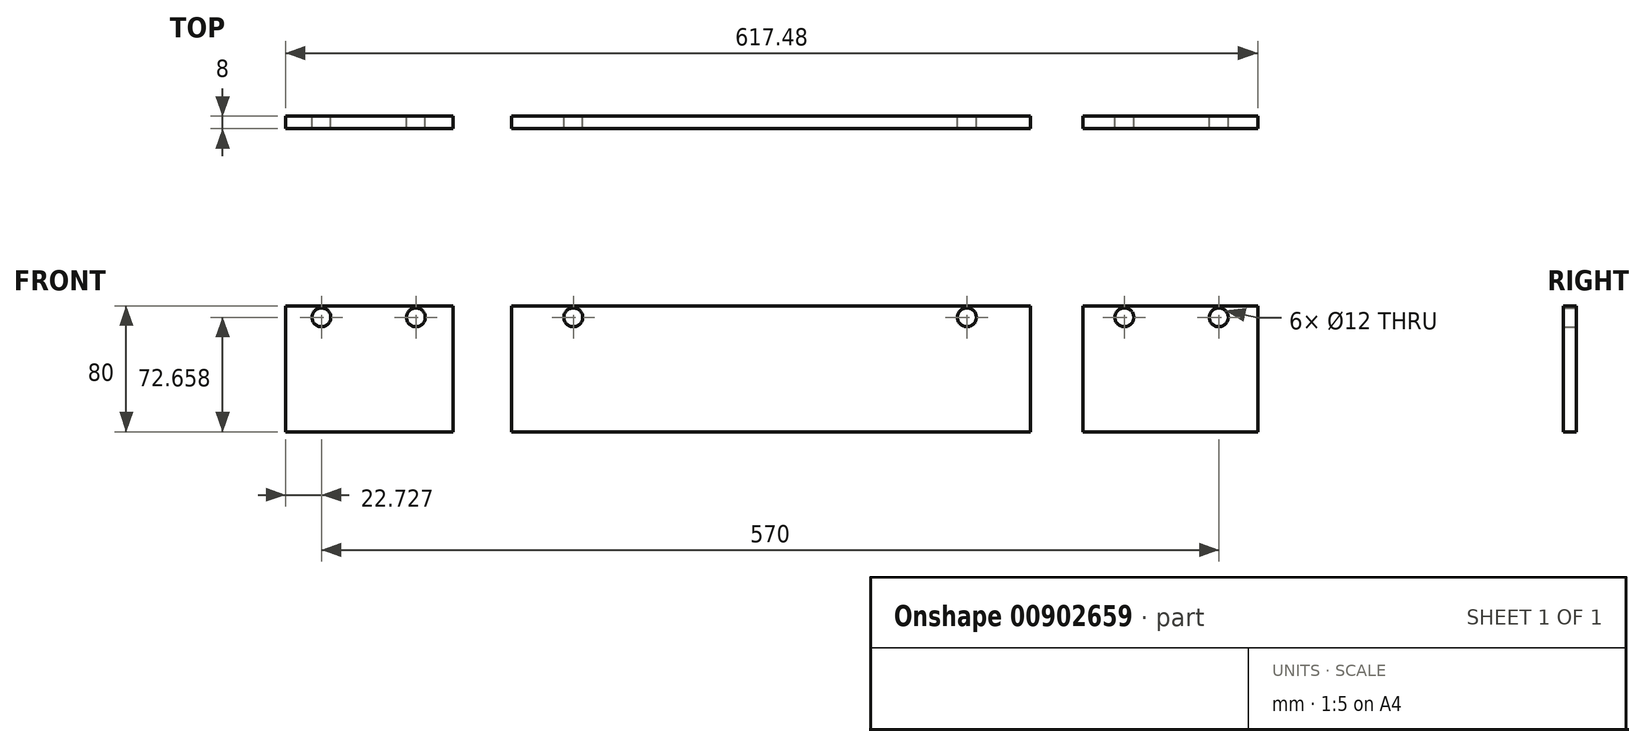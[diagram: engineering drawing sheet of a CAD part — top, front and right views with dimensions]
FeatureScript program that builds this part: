
annotation { "Feature Type Name" : "Feature", "Feature Type Description" : "" }
export const myFeature = defineFeature(function(context is Context, id is Id, definition is map)
    precondition{}
    {
        {
            var Q0;
            Q0=qCreatedBy(makeId("Front.planeOp"),FACE);
            var sketch = newSketch(context, id + "F0", { "sketchPlane" : qUnion([Q0])});
            skCircle(sketch, "E0", {"center": v(-315.46, 41.45) * mm, "radius": 6 * mm});
            skCircle(sketch, "E1", {"center": v(-255.46, 41.45) * mm, "radius": 6 * mm});
            skCircle(sketch, "E2", {"center": v(-155.46, 41.45) * mm, "radius": 6 * mm});
            skCircle(sketch, "E3", {"center": v(94.54, 41.45) * mm, "radius": 6 * mm});
            skCircle(sketch, "E4", {"center": v(194.54, 41.45) * mm, "radius": 6 * mm});
            skCircle(sketch, "E5", {"center": v(254.54, 41.45) * mm, "radius": 6 * mm});
            skLineSegment(sketch, "E6.bottom", {"start": v(-338.19, 48.79) * mm, "end": v(-231.92, 48.79) * mm});
            skLineSegment(sketch, "E6.top", {"start": v(-338.19, -31.21) * mm, "end": v(-231.92, -31.21) * mm});
            skLineSegment(sketch, "E6.left", {"start": v(-338.19, 48.79) * mm, "end": v(-338.19, -31.21) * mm});
            skLineSegment(sketch, "E6.right", {"start": v(-231.92, 48.79) * mm, "end": v(-231.92, -31.21) * mm});
            skLineSegment(sketch, "E7.bottom", {"start": v(-194.59, 48.79) * mm, "end": v(134.73, 48.79) * mm});
            skLineSegment(sketch, "E7.top", {"start": v(-194.59, -31.21) * mm, "end": v(134.73, -31.21) * mm});
            skLineSegment(sketch, "E7.left", {"start": v(-194.59, 48.79) * mm, "end": v(-194.59, -31.21) * mm});
            skLineSegment(sketch, "E7.right", {"start": v(134.73, 48.79) * mm, "end": v(134.73, -31.21) * mm});
            skLineSegment(sketch, "E8.bottom", {"start": v(168.24, 48.79) * mm, "end": v(279.29, 48.79) * mm});
            skLineSegment(sketch, "E8.top", {"start": v(168.24, -31.21) * mm, "end": v(279.29, -31.21) * mm});
            skLineSegment(sketch, "E8.left", {"start": v(168.24, 48.79) * mm, "end": v(168.24, -31.21) * mm});
            skLineSegment(sketch, "E8.right", {"start": v(279.29, 48.79) * mm, "end": v(279.29, -31.21) * mm});
            skSolve(sketch);
        }
        {
            var Q0;
            Q0 = qSketchRegion(id + "F0", true);
            extrude(context, id + "F1", {"entities" : qUnion([Q0]), "depth" : 8 * mm, "offsetDistance" : 25 * mm});
        }
    });
